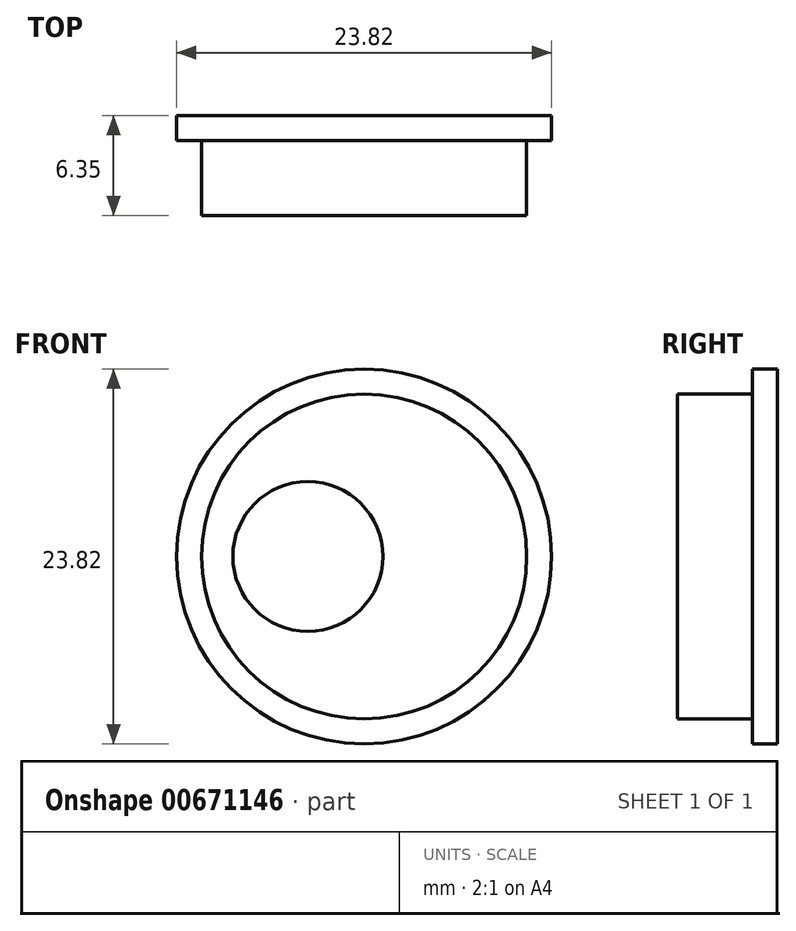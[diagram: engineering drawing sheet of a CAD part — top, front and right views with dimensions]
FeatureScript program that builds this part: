
annotation { "Feature Type Name" : "Feature", "Feature Type Description" : "" }
export const myFeature = defineFeature(function(context is Context, id is Id, definition is map)
    precondition{}
    {
        {
            var Q0;
            Q0=qCreatedBy(makeId("Front.planeOp"),FACE);
            var sketch = newSketch(context, id + "F0", { "sketchPlane" : qUnion([Q0])});
            skCircle(sketch, "E0", {"center": v(0, 0) * mm, "radius": 11.9 * mm});
            skSolve(sketch);
        }
        {
            var Q0;
            Q0=qSketchRegion(id+"F0",true);
            extrude(context, id + "F1", {"entities" : qUnion([Q0]), "depth" : 1.59 * mm});
        }
        {
            var Q0;
            Q0=makeQuery(id+"F1.opExtrude","CAP_FACE",FACE,{"disambiguationData":[OSD([sQuery(id+"F0.wireOp",EDGE,"E0")])],"isStart":false});
            var sketch = newSketch(context, id + "F2", { "sketchPlane" : qUnion([Q0])});
            skCircle(sketch, "E1", {"center": v(0, 0) * mm, "radius": 10.32 * mm});
            skSolve(sketch);
        }
        {
            var Q0;
            Q0=qSketchRegion(id+"F2",true);
            extrude(context, id + "F3", {"entities" : qUnion([Q0]), "operationType" : NewBodyOperationType.ADD, "depth" : 4.76 * mm});
        }
        {
            var Q0;
            Q0=makeQuery(id+"F3.opExtrude","CAP_FACE",FACE,{"disambiguationData":[OSD([sQuery(id+"F2.wireOp",EDGE,"E1")])],"isStart":false});
            var sketch = newSketch(context, id + "F4", { "sketchPlane" : qUnion([Q0])});
            skCircle(sketch, "E2", {"center": v(-3.57, 0) * mm, "radius": 4.76 * mm});
            skSolve(sketch);
        }
        {
            var Q0;
            Q0=qSketchRegion(id+"F4",true);
            extrude(context, id + "F5", {"entities" : qUnion([Q0]), "operationType" : NewBodyOperationType.ADD, "depth" : 1 / 203.2 * mm});
        }
    });
